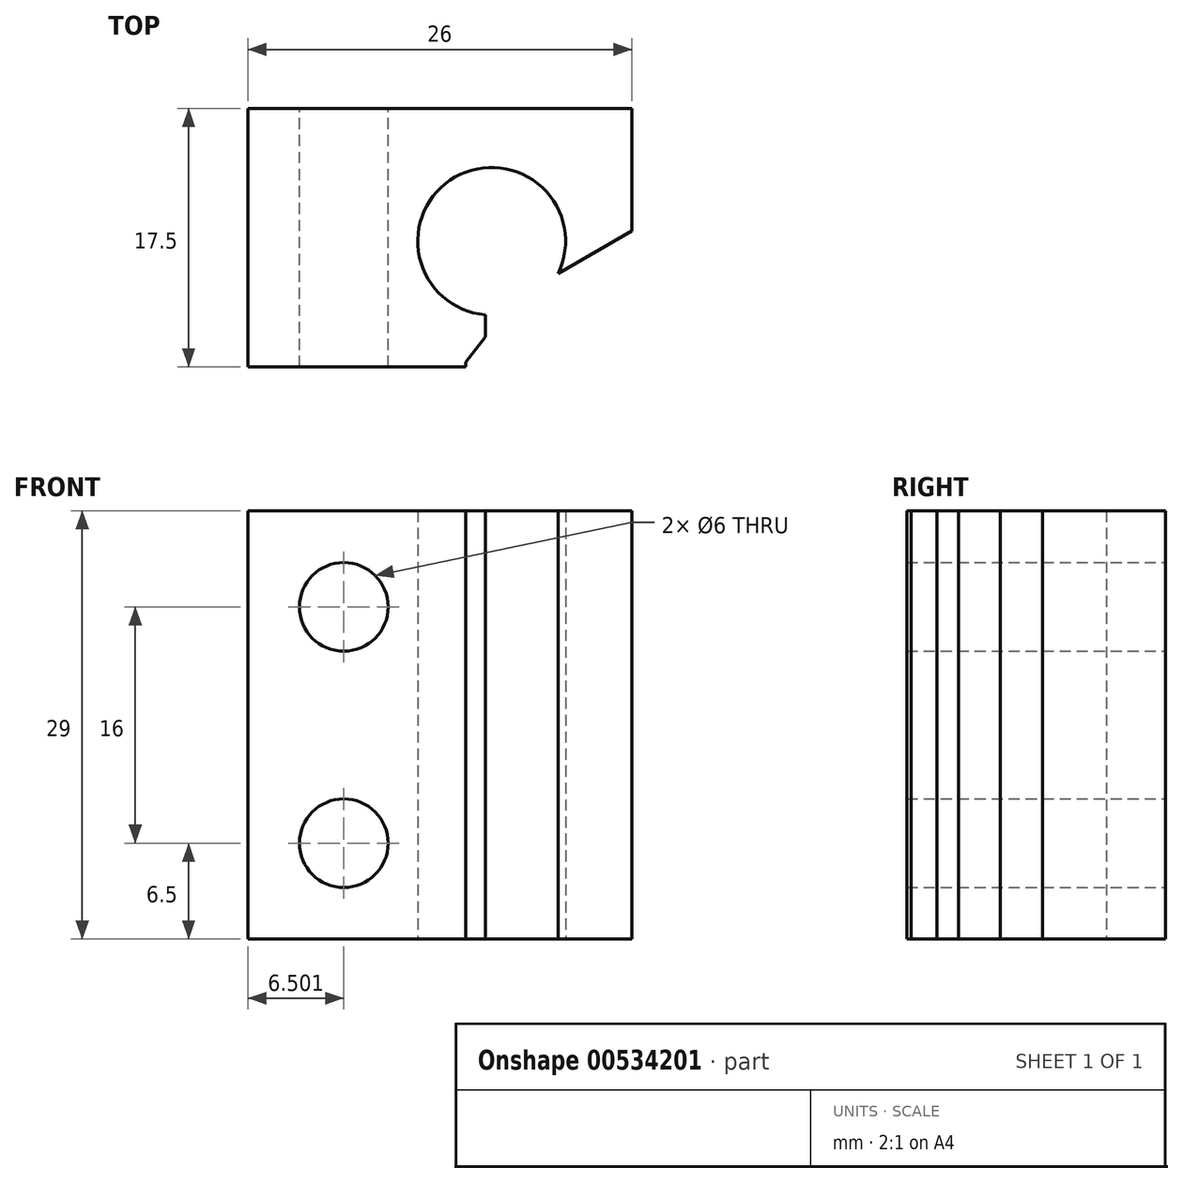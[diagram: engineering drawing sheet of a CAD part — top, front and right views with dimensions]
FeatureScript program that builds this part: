
annotation { "Feature Type Name" : "Feature", "Feature Type Description" : "" }
export const myFeature = defineFeature(function(context is Context, id is Id, definition is map)
    precondition{}
    {
        {
            var Q0;
            Q0=qCreatedBy(makeId("Top.planeOp"),FACE);
            var sketch = newSketch(context, id + "F0", { "sketchPlane" : qUnion([Q0])});
            skArc(sketch, "E0", {"start": v(6.34, -0.44) * mm, "mid": v(-0.64, 6.07) * mm, "end": v(1.4, -3.25) * mm});
            skLineSegment(sketch, "E1", {"start": v(-14.67, -6.77) * mm, "end": v(-14.67, 10.73) * mm});
            skLineSegment(sketch, "E2", {"start": v(-14.67, 10.73) * mm, "end": v(11.33, 10.73) * mm});
            skLineSegment(sketch, "E3", {"start": v(11.33, 10.73) * mm, "end": v(11.33, 2.42) * mm});
            skLineSegment(sketch, "E4", {"start": v(11.33, 2.42) * mm, "end": v(6.34, -0.44) * mm});
            skLineSegment(sketch, "E5", {"start": v(1.4, -3.25) * mm, "end": v(1.4, -4.73) * mm});
            skLineSegment(sketch, "E6", {"start": v(1.4, -4.73) * mm, "end": v(0.07, -6.47) * mm});
            skLineSegment(sketch, "E7", {"start": v(0.07, -6.47) * mm, "end": v(0.07, -6.77) * mm});
            skLineSegment(sketch, "E8", {"start": v(0.07, -6.77) * mm, "end": v(-14.67, -6.77) * mm});
            skSolve(sketch);
        }
        {
            var Q0;
            Q0=makeQuery(id+"F0.imprint","IMPRINT",FACE,{"disambiguationData":[TD([[makeQuery(id+"F0.imprint","IMPRINT",EDGE,{"derivedFrom":sQuery(id+"F0.wireOp",EDGE,"E0")}),-1.0]])]});
            extrude(context, id + "F1", {"entities" : qUnion([Q0]), "depth" : 29 * mm, "offsetDistance" : 25 * mm});
        }
        {
            var Q0;
            Q0=makeQuery(id+"F1.opExtrude","SWEPT_FACE",FACE,{"disambiguationData":[OSD([sQuery(id+"F0.wireOp",EDGE,"E2")])]});
            var sketch = newSketch(context, id + "F2", { "sketchPlane" : qUnion([Q0])});
            skLineSegment(sketch, "E9", {"start": v(14.67, 29) * mm, "end": v(8.17, 29) * mm, "construction": true});
            skLineSegment(sketch, "E10", {"start": v(8.17, 29) * mm, "end": v(8.17, 0) * mm, "construction": true});
            skLineSegment(sketch, "E11", {"start": v(8.17, 29) * mm, "end": v(8.17, 14.5) * mm, "construction": true});
            skLineSegment(sketch, "E12", {"start": v(8.17, 14.5) * mm, "end": v(8.17, 22.5) * mm, "construction": true});
            skLineSegment(sketch, "E13", {"start": v(8.17, 14.5) * mm, "end": v(8.17, 6.5) * mm, "construction": true});
            skCircle(sketch, "E14", {"center": v(8.17, 22.5) * mm, "radius": 3 * mm});
            skCircle(sketch, "E15", {"center": v(8.17, 6.5) * mm, "radius": 3 * mm});
            skSolve(sketch);
        }
        {
            var Q0;
            Q0=makeQuery(id+"F2.imprint","IMPRINT",FACE,{"disambiguationData":[TD([[makeQuery(id+"F2.imprint","IMPRINT",EDGE,{"derivedFrom":sQuery(id+"F2.wireOp",EDGE,"E14")}),1.0]])]});
            var Q1;
            Q1=makeQuery(id+"F2.imprint","IMPRINT",FACE,{"disambiguationData":[TD([[makeQuery(id+"F2.imprint","IMPRINT",EDGE,{"derivedFrom":sQuery(id+"F2.wireOp",EDGE,"E15")}),1.0]])]});
            extrude(context, id + "F3", {"entities" : qUnion([Q0, Q1]), "operationType" : NewBodyOperationType.REMOVE, "endBound" : BoundingType.THROUGH_ALL, "oppositeDirection" : true, "depth" : 25 * mm, "offsetDistance" : 25 * mm});
        }
    });
